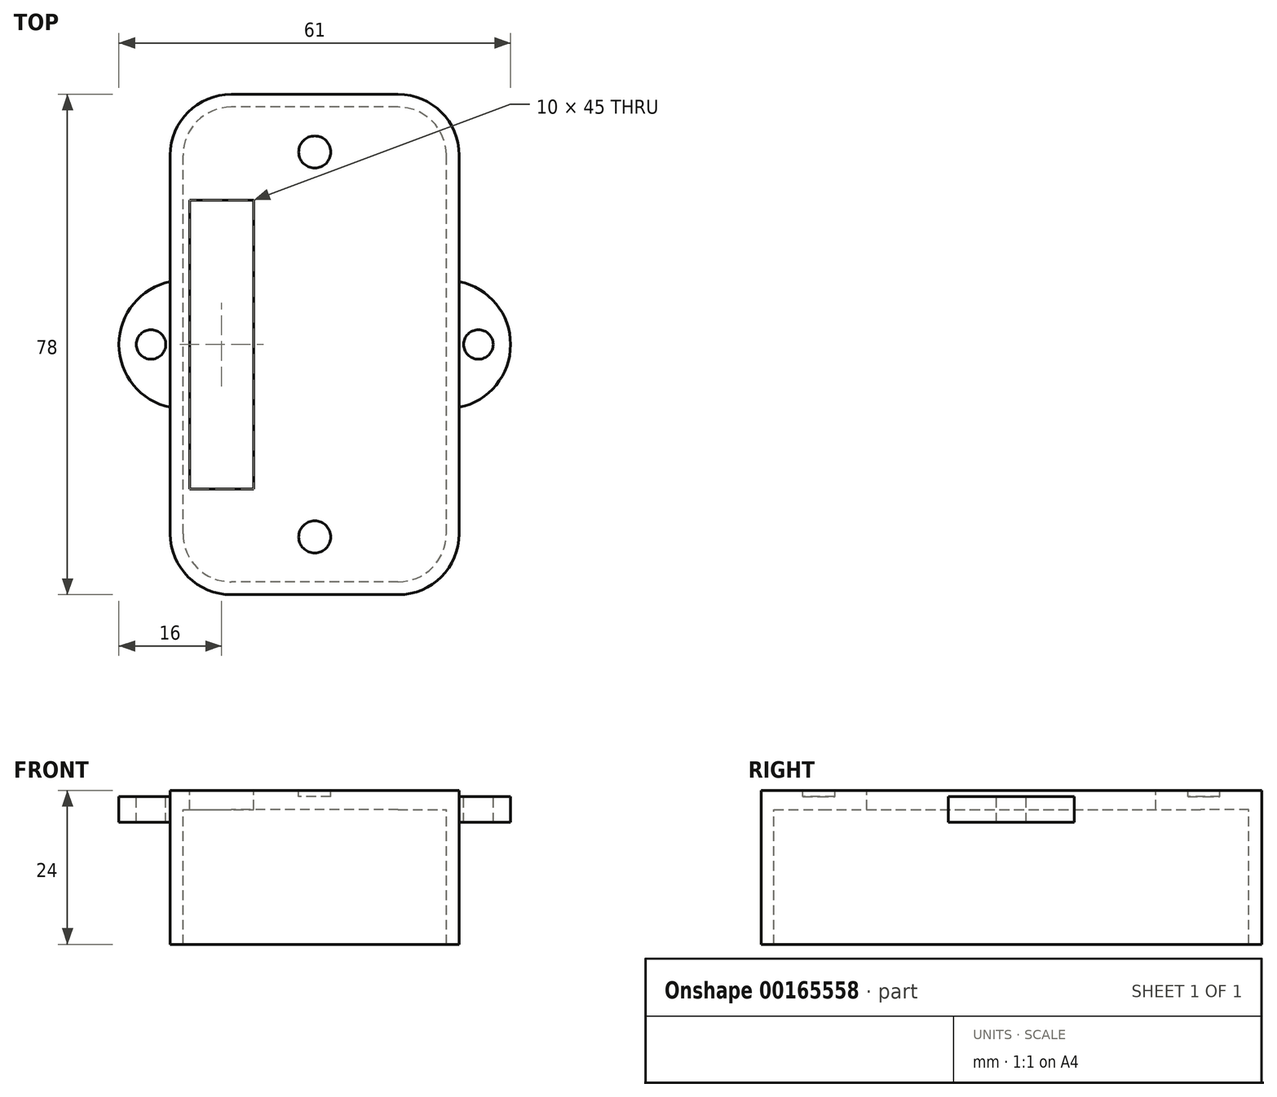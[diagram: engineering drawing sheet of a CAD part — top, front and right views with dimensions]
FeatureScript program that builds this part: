
annotation { "Feature Type Name" : "Feature", "Feature Type Description" : "" }
export const myFeature = defineFeature(function(context is Context, id is Id, definition is map)
    precondition{}
    {
        {
            var Q0;
            Q0=qCreatedBy(makeId("Top.planeOp"),FACE);
            var sketch = newSketch(context, id + "F0", { "sketchPlane" : qUnion([Q0])});
            skLineSegment(sketch, "E0.bottom", {"start": v(13, -37) * mm, "end": v(-13, -37) * mm});
            skLineSegment(sketch, "E0.top", {"start": v(13, 37) * mm, "end": v(-13, 37) * mm});
            skLineSegment(sketch, "E0.left", {"start": v(20.5, -29.5) * mm, "end": v(20.5, 29.5) * mm});
            skLineSegment(sketch, "E0.right", {"start": v(-20.5, -29.5) * mm, "end": v(-20.5, 29.5) * mm});
            skPoint(sketch, "E0.middle", {"position": v(0, 0) * mm});
            skPoint(sketch, "E1.visualSharp", {"position": v(-20.5, 37) * mm});
            skArc(sketch, "E1.filletArc", {"start": v(-13, 37) * mm, "mid": v(-18.3, 34.8) * mm, "end": v(-20.5, 29.5) * mm});
            skPoint(sketch, "E2.visualSharp", {"position": v(20.5, 37) * mm});
            skArc(sketch, "E2.filletArc", {"start": v(20.5, 29.5) * mm, "mid": v(18.3, 34.8) * mm, "end": v(13, 37) * mm});
            skPoint(sketch, "E3.visualSharp", {"position": v(20.5, -37) * mm});
            skArc(sketch, "E3.filletArc", {"start": v(13, -37) * mm, "mid": v(18.3, -34.8) * mm, "end": v(20.5, -29.5) * mm});
            skPoint(sketch, "E4.visualSharp", {"position": v(-20.5, -37) * mm});
            skArc(sketch, "E4.filletArc", {"start": v(-20.5, -29.5) * mm, "mid": v(-18.3, -34.8) * mm, "end": v(-13, -37) * mm});
            skArc(sketch, "E5.0", {"start": v(-22.5, -29.5) * mm, "mid": v(-19.72, -36.22) * mm, "end": v(-13, -39) * mm});
            skLineSegment(sketch, "E5.1", {"start": v(13, -39) * mm, "end": v(-13, -39) * mm});
            skLineSegment(sketch, "E5.2", {"start": v(-22.5, -29.5) * mm, "end": v(-22.5, 29.5) * mm});
            skArc(sketch, "E5.3", {"start": v(13, -39) * mm, "mid": v(19.72, -36.22) * mm, "end": v(22.5, -29.5) * mm});
            skArc(sketch, "E5.4", {"start": v(-13, 39) * mm, "mid": v(-19.72, 36.22) * mm, "end": v(-22.5, 29.5) * mm});
            skLineSegment(sketch, "E5.5", {"start": v(13, 39) * mm, "end": v(-13, 39) * mm});
            skArc(sketch, "E5.6", {"start": v(22.5, 29.5) * mm, "mid": v(19.72, 36.22) * mm, "end": v(13, 39) * mm});
            skLineSegment(sketch, "E5.7", {"start": v(22.5, -29.5) * mm, "end": v(22.5, 29.5) * mm});
            skPoint(sketch, "E6.centerSnap0", {"position": v(20.5, 0) * mm});
            skLineSegment(sketch, "E7", {"start": v(0, 0) * mm, "end": v(0, -30) * mm});
            skCircle(sketch, "E8", {"center": v(0, -30) * mm, "radius": 2.5 * mm});
            skCircle(sketch, "E9", {"center": v(0, 30) * mm, "radius": 2.5 * mm});
            skLineSegment(sketch, "E10.0", {"start": v(-19.5, 0) * mm, "end": v(-19.5, -22.5) * mm});
            skLineSegment(sketch, "E10.1", {"start": v(-19.5, 0) * mm, "end": v(-19.5, 22.5) * mm});
            skLineSegment(sketch, "E11.0", {"start": v(-9.5, 0) * mm, "end": v(-9.5, -22.5) * mm});
            skLineSegment(sketch, "E11.1", {"start": v(-9.5, 0) * mm, "end": v(-9.5, 22.5) * mm});
            skLineSegment(sketch, "E12", {"start": v(-19.5, 22.5) * mm, "end": v(-9.5, 22.5) * mm});
            skLineSegment(sketch, "E13", {"start": v(-19.5, -22.5) * mm, "end": v(-9.5, -22.5) * mm});
            skArc(sketch, "E14", {"start": v(22.5, -9.8) * mm, "mid": v(30.5, 0) * mm, "end": v(22.5, 9.8) * mm});
            skLineSegment(sketch, "E15", {"start": v(20.5, 0) * mm, "end": v(30.5, 0) * mm, "construction": true});
            skLineSegment(sketch, "E16", {"start": v(22.5, 0) * mm, "end": v(25.5, 0) * mm});
            skArc(sketch, "E17.MirrorCS", {"start": v(-22.5, -9.8) * mm, "mid": v(-30.5, 0) * mm, "end": v(-22.5, 9.8) * mm});
            skCircle(sketch, "E18", {"center": v(25.5, 0) * mm, "radius": 2.3 * mm});
            skCircle(sketch, "E19.MirrorC", {"center": v(-25.5, 0) * mm, "radius": 2.3 * mm});
            skSolve(sketch);
        }
        {
            var Q0;
            {var subQ5=sQuery(id+"F0.wireOp",EDGE,"K4ufOepT-8zNa-qbsu-fNWP-Ed5ITKJvoy9s.right");Q0=makeQuery(id+"F0.imprint","IMPRINT",FACE,{"disambiguationData":[TD([[makeQuery(id+"F0.imprint","IMPRINT",EDGE,{"derivedFrom":subQ5}),-1.0]])]});}
            var Q1;
            Q1=makeQuery(id+"F0.imprint","IMPRINT",FACE,{"disambiguationData":[TD([[makeQuery(id+"F0.imprint","IMPRINT",EDGE,{"derivedFrom":sQuery(id+"F0.wireOp",EDGE,"E0.top")}),1.0]])]});
            var Q2;
            Q2=makeQuery(id+"F0.imprint","IMPRINT",FACE,{"disambiguationData":[TD([[makeQuery(id+"F0.imprint","IMPRINT",EDGE,{"derivedFrom":sQuery(id+"F0.wireOp",EDGE,"E0.bottom")}),-1.0]])]});
            var Q3;
            {var subQ1=sQuery(id+"F0.wireOp",EDGE,"K4ufOepT-8zNa-qbsu-fNWP-Ed5ITKJvoy9s.left");var subQ3=sQuery(id+"F0.wireOp",EDGE,"29d169b9-53f3-4a3d-8caf-3cd1a107282e.0");var subQ4=makeQuery(id+"F0.imprint","INTERSECT",VERTEX,{"derivedFrom":[subQ3,subQ1]});Q3=makeQuery(id+"F0.imprint","IMPRINT",FACE,{"disambiguationData":[TD([[makeQuery(id+"F0.imprint","IMPRINT",EDGE,{"disambiguationData":[TD([[subQ4,-1.0]])],"derivedFrom":subQ3}),1.0]])]});}
            var Q4;
            {var subQ5=sQuery(id+"F0.wireOp",EDGE,"E0.right");var subQ6=sQuery(id+"F0.wireOp",EDGE,"rMVOqYj8-UWur-ThiU-V0Ca-l3qG7JqcSif2");var subQ7=makeQuery(id+"F0.imprint","INTERSECT",VERTEX,{"disambiguationData":[OD(1.0)],"derivedFrom":[subQ6,subQ5]});Q4=makeQuery(id+"F0.imprint","IMPRINT",FACE,{"disambiguationData":[TD([[makeQuery(id+"F0.imprint","IMPRINT",EDGE,{"disambiguationData":[TD([[subQ7,-1.0]])],"derivedFrom":subQ6}),1.0]])]});}
            var Q5;
            {var subQ6=sQuery(id+"F0.wireOp",EDGE,"rMVOqYj8-UWur-ThiU-V0Ca-l3qG7JqcSif2");var subQ11=sQuery(id+"F0.wireOp",EDGE,"E9");var subQ12=makeQuery(id+"F0.imprint","INTERSECT",VERTEX,{"disambiguationData":[OD(1.0)],"derivedFrom":[subQ6,subQ11]});Q5=makeQuery(id+"F0.imprint","IMPRINT",FACE,{"disambiguationData":[TD([[makeQuery(id+"F0.imprint","IMPRINT",EDGE,{"disambiguationData":[TD([[subQ12,-1.0]])],"derivedFrom":subQ6}),1.0]])]});}
            var Q6;
            {var subQ0=sQuery(id+"F0.wireOp",EDGE,"NyWOWrau-7Y7n-SZSj-ABbT-IQbbcggIcJFY");var subQ1=sQuery(id+"F0.wireOp",EDGE,"29d169b9-53f3-4a3d-8caf-3cd1a107282e.0");var subQ2=makeQuery(id+"F0.imprint","INTERSECT",VERTEX,{"disambiguationData":[OD(0.0)],"derivedFrom":[subQ1,subQ0]});Q6=makeQuery(id+"F0.imprint","IMPRINT",FACE,{"disambiguationData":[TD([[makeQuery(id+"F0.imprint","IMPRINT",EDGE,{"disambiguationData":[TD([[subQ2,-1.0]])],"derivedFrom":subQ1}),1.0]])]});}
            var Q7;
            {var subQ0=sQuery(id+"F0.wireOp",EDGE,"E9");var subQ1=sQuery(id+"F0.wireOp",EDGE,"McuKKnwl-45qK-wBoD-dtIe-04McT4cX6IDA");var subQ2=makeQuery(id+"F0.imprint","INTERSECT",VERTEX,{"disambiguationData":[OD(0.0)],"derivedFrom":[subQ1,subQ0]});Q7=makeQuery(id+"F0.imprint","IMPRINT",FACE,{"disambiguationData":[TD([[makeQuery(id+"F0.imprint","IMPRINT",EDGE,{"disambiguationData":[TD([[subQ2,1.0]])],"derivedFrom":subQ1}),1.0]])]});}
            var Q8;
            {var subQ0=sQuery(id+"F0.wireOp",EDGE,"E9");var subQ1=sQuery(id+"F0.wireOp",EDGE,"29d169b9-53f3-4a3d-8caf-3cd1a107282e.0");var subQ2=makeQuery(id+"F0.imprint","INTERSECT",VERTEX,{"disambiguationData":[OD(1.0)],"derivedFrom":[subQ1,subQ0]});Q8=makeQuery(id+"F0.imprint","IMPRINT",FACE,{"disambiguationData":[TD([[makeQuery(id+"F0.imprint","IMPRINT",EDGE,{"disambiguationData":[TD([[subQ2,-1.0]])],"derivedFrom":subQ1}),-1.0]])]});}
            var Q9;
            {var subQ0=sQuery(id+"F0.wireOp",EDGE,"NyWOWrau-7Y7n-SZSj-ABbT-IQbbcggIcJFY");var subQ1=sQuery(id+"F0.wireOp",EDGE,"29d169b9-53f3-4a3d-8caf-3cd1a107282e.0");var subQ2=makeQuery(id+"F0.imprint","INTERSECT",VERTEX,{"disambiguationData":[OD(0.0)],"derivedFrom":[subQ1,subQ0]});Q9=makeQuery(id+"F0.imprint","IMPRINT",FACE,{"disambiguationData":[TD([[makeQuery(id+"F0.imprint","IMPRINT",EDGE,{"disambiguationData":[TD([[subQ2,-1.0]])],"derivedFrom":subQ1}),-1.0]])]});}
            var Q10;
            {var subQ0=sQuery(id+"F0.wireOp",EDGE,"E9");var subQ1=sQuery(id+"F0.wireOp",EDGE,"rMVOqYj8-UWur-ThiU-V0Ca-l3qG7JqcSif2");var subQ2=makeQuery(id+"F0.imprint","INTERSECT",VERTEX,{"disambiguationData":[OD(1.0)],"derivedFrom":[subQ1,subQ0]});Q10=makeQuery(id+"F0.imprint","IMPRINT",FACE,{"disambiguationData":[TD([[makeQuery(id+"F0.imprint","IMPRINT",EDGE,{"disambiguationData":[TD([[subQ2,-1.0]])],"derivedFrom":subQ1}),-1.0]])]});}
            var Q11;
            {var subQ0=sQuery(id+"F0.wireOp",EDGE,"E0.left");var subQ1=sQuery(id+"F0.wireOp",EDGE,"rMVOqYj8-UWur-ThiU-V0Ca-l3qG7JqcSif2");var subQ2=makeQuery(id+"F0.imprint","INTERSECT",VERTEX,{"disambiguationData":[OD(0.0)],"derivedFrom":[subQ1,subQ0]});Q11=makeQuery(id+"F0.imprint","IMPRINT",FACE,{"disambiguationData":[TD([[makeQuery(id+"F0.imprint","IMPRINT",EDGE,{"disambiguationData":[TD([[subQ2,-1.0]])],"derivedFrom":subQ1}),-1.0]])]});}
            var Q12;
            {var subQ5=sQuery(id+"F0.wireOp",EDGE,"E0.left");var subQ6=sQuery(id+"F0.wireOp",EDGE,"rMVOqYj8-UWur-ThiU-V0Ca-l3qG7JqcSif2");var subQ7=makeQuery(id+"F0.imprint","INTERSECT",VERTEX,{"disambiguationData":[OD(0.0)],"derivedFrom":[subQ6,subQ5]});Q12=makeQuery(id+"F0.imprint","IMPRINT",FACE,{"disambiguationData":[TD([[makeQuery(id+"F0.imprint","IMPRINT",EDGE,{"disambiguationData":[TD([[subQ7,-1.0]])],"derivedFrom":subQ6}),1.0]])]});}
            var Q13;
            {var subQ0=sQuery(id+"F0.wireOp",EDGE,"E8");var subQ1=sQuery(id+"F0.wireOp",EDGE,"rMVOqYj8-UWur-ThiU-V0Ca-l3qG7JqcSif2");var subQ2=makeQuery(id+"F0.imprint","INTERSECT",VERTEX,{"disambiguationData":[OD(1.0)],"derivedFrom":[subQ1,subQ0]});Q13=makeQuery(id+"F0.imprint","IMPRINT",FACE,{"disambiguationData":[TD([[makeQuery(id+"F0.imprint","IMPRINT",EDGE,{"disambiguationData":[TD([[subQ2,-1.0]])],"derivedFrom":subQ1}),-1.0]])]});}
            var Q14;
            {var subQ3=sQuery(id+"F0.wireOp",EDGE,"E8");var subQ6=sQuery(id+"F0.wireOp",EDGE,"rMVOqYj8-UWur-ThiU-V0Ca-l3qG7JqcSif2");var subQ9=makeQuery(id+"F0.imprint","INTERSECT",VERTEX,{"disambiguationData":[OD(1.0)],"derivedFrom":[subQ6,subQ3]});Q14=makeQuery(id+"F0.imprint","IMPRINT",FACE,{"disambiguationData":[TD([[makeQuery(id+"F0.imprint","IMPRINT",EDGE,{"disambiguationData":[TD([[subQ9,-1.0]])],"derivedFrom":subQ6}),1.0]])]});}
            var Q15;
            {var subQ5=sQuery(id+"F0.wireOp",EDGE,"29d169b9-53f3-4a3d-8caf-3cd1a107282e.0");var subQ7=sQuery(id+"F0.wireOp",EDGE,"E8");var subQ9=makeQuery(id+"F0.imprint","INTERSECT",VERTEX,{"disambiguationData":[OD(1.0)],"derivedFrom":[subQ5,subQ7]});Q15=makeQuery(id+"F0.imprint","IMPRINT",FACE,{"disambiguationData":[TD([[makeQuery(id+"F0.imprint","IMPRINT",EDGE,{"disambiguationData":[TD([[subQ9,-1.0]])],"derivedFrom":subQ5}),1.0]])]});}
            var Q16;
            {var subQ0=sQuery(id+"F0.wireOp",EDGE,"E0.right");var subQ1=sQuery(id+"F0.wireOp",EDGE,"rMVOqYj8-UWur-ThiU-V0Ca-l3qG7JqcSif2");var subQ2=makeQuery(id+"F0.imprint","INTERSECT",VERTEX,{"disambiguationData":[OD(1.0)],"derivedFrom":[subQ1,subQ0]});Q16=makeQuery(id+"F0.imprint","IMPRINT",FACE,{"disambiguationData":[TD([[makeQuery(id+"F0.imprint","IMPRINT",EDGE,{"disambiguationData":[TD([[subQ2,-1.0]])],"derivedFrom":subQ1}),-1.0]])]});}
            var Q17;
            {var subQ0=sQuery(id+"F0.wireOp",EDGE,"E8");var subQ1=sQuery(id+"F0.wireOp",EDGE,"29d169b9-53f3-4a3d-8caf-3cd1a107282e.0");var subQ2=makeQuery(id+"F0.imprint","INTERSECT",VERTEX,{"disambiguationData":[OD(1.0)],"derivedFrom":[subQ1,subQ0]});Q17=makeQuery(id+"F0.imprint","IMPRINT",FACE,{"disambiguationData":[TD([[makeQuery(id+"F0.imprint","IMPRINT",EDGE,{"disambiguationData":[TD([[subQ2,-1.0]])],"derivedFrom":subQ1}),-1.0]])]});}
            var Q18;
            {var subQ0=sQuery(id+"F0.wireOp",EDGE,"eekdeFhl-0S7z-osEv-NQff-r2qTQL0hCeFo");var subQ1=sQuery(id+"F0.wireOp",EDGE,"29d169b9-53f3-4a3d-8caf-3cd1a107282e.0");var subQ2=makeQuery(id+"F0.imprint","INTERSECT",VERTEX,{"disambiguationData":[OD(0.0)],"derivedFrom":[subQ1,subQ0]});Q18=makeQuery(id+"F0.imprint","IMPRINT",FACE,{"disambiguationData":[TD([[makeQuery(id+"F0.imprint","IMPRINT",EDGE,{"disambiguationData":[TD([[subQ2,-1.0]])],"derivedFrom":subQ1}),-1.0]])]});}
            var Q19;
            {var subQ1=sQuery(id+"F0.wireOp",EDGE,"eekdeFhl-0S7z-osEv-NQff-r2qTQL0hCeFo");var subQ3=sQuery(id+"F0.wireOp",EDGE,"29d169b9-53f3-4a3d-8caf-3cd1a107282e.0");var subQ4=makeQuery(id+"F0.imprint","INTERSECT",VERTEX,{"disambiguationData":[OD(0.0)],"derivedFrom":[subQ3,subQ1]});Q19=makeQuery(id+"F0.imprint","IMPRINT",FACE,{"disambiguationData":[TD([[makeQuery(id+"F0.imprint","IMPRINT",EDGE,{"disambiguationData":[TD([[subQ4,-1.0]])],"derivedFrom":subQ3}),1.0]])]});}
            var Q20;
            {var subQ0=sQuery(id+"F0.wireOp",EDGE,"E8");var subQ1=sQuery(id+"F0.wireOp",EDGE,"gFNWuceC-rtio-qrhw-MDK2-LZ9uLdkySnU5");var subQ2=makeQuery(id+"F0.imprint","INTERSECT",VERTEX,{"disambiguationData":[OD(0.0)],"derivedFrom":[subQ1,subQ0]});Q20=makeQuery(id+"F0.imprint","IMPRINT",FACE,{"disambiguationData":[TD([[makeQuery(id+"F0.imprint","IMPRINT",EDGE,{"disambiguationData":[TD([[subQ2,1.0]])],"derivedFrom":subQ1}),1.0]])]});}
            var Q21;
            {var subQ0=sQuery(id+"F0.wireOp",EDGE,"E7");var subQ1=sQuery(id+"F0.wireOp",EDGE,"gFNWuceC-rtio-qrhw-MDK2-LZ9uLdkySnU5");var subQ2=makeQuery(id+"F0.imprint","INTERSECT",VERTEX,{"derivedFrom":[subQ1,subQ0]});Q21=makeQuery(id+"F0.imprint","IMPRINT",FACE,{"disambiguationData":[TD([[makeQuery(id+"F0.imprint","IMPRINT",EDGE,{"disambiguationData":[TD([[subQ2,1.0]])],"derivedFrom":subQ1}),1.0]])]});}
            extrude(context, id + "F1", {"entities" : qUnion([Q0, Q1, Q2, Q3, Q4, Q5, Q6, Q7, Q8, Q9, Q10, Q11, Q12, Q13, Q14, Q15, Q16, Q17, Q18, Q19, Q20, Q21]), "oppositeDirection" : true, "depth" : 2 * mm});
        }
        {
            var Q0;
            Q0=makeQuery(id+"F0.imprint","IMPRINT",FACE,{"disambiguationData":[TD([[makeQuery(id+"F0.imprint","IMPRINT",EDGE,{"derivedFrom":sQuery(id+"F0.wireOp",EDGE,"E0.top")}),-1.0]])]});
            var Q1;
            {var subQ0=sQuery(id+"F0.wireOp",EDGE,"E5.7");var subQ1=sQuery(id+"F0.wireOp",EDGE,"29d169b9-53f3-4a3d-8caf-3cd1a107282e.0");var subQ2=makeQuery(id+"F0.imprint","INTERSECT",VERTEX,{"disambiguationData":[OD(0.0)],"derivedFrom":[subQ1,subQ0]});Q1=makeQuery(id+"F0.imprint","IMPRINT",FACE,{"disambiguationData":[TD([[makeQuery(id+"F0.imprint","IMPRINT",EDGE,{"disambiguationData":[TD([[subQ2,-1.0]])],"derivedFrom":subQ1}),1.0]])]});}
            var Q2;
            {var subQ0=sQuery(id+"F0.wireOp",EDGE,"E0.left");var subQ1=sQuery(id+"F0.wireOp",EDGE,"rMVOqYj8-UWur-ThiU-V0Ca-l3qG7JqcSif2");var subQ2=makeQuery(id+"F0.imprint","INTERSECT",VERTEX,{"disambiguationData":[OD(0.0)],"derivedFrom":[subQ1,subQ0]});Q2=makeQuery(id+"F0.imprint","IMPRINT",FACE,{"disambiguationData":[TD([[makeQuery(id+"F0.imprint","IMPRINT",EDGE,{"disambiguationData":[TD([[subQ2,1.0]])],"derivedFrom":subQ1}),1.0]])]});}
            var Q3;
            {var subQ0=sQuery(id+"F0.wireOp",EDGE,"E0.left");var subQ1=sQuery(id+"F0.wireOp",EDGE,"rMVOqYj8-UWur-ThiU-V0Ca-l3qG7JqcSif2");var subQ2=makeQuery(id+"F0.imprint","INTERSECT",VERTEX,{"disambiguationData":[OD(0.0)],"derivedFrom":[subQ1,subQ0]});Q3=makeQuery(id+"F0.imprint","IMPRINT",FACE,{"disambiguationData":[TD([[makeQuery(id+"F0.imprint","IMPRINT",EDGE,{"disambiguationData":[TD([[subQ2,1.0]])],"derivedFrom":subQ1}),-1.0]])]});}
            var Q4;
            {var subQ0=sQuery(id+"F0.wireOp",EDGE,"E0.left");var subQ1=sQuery(id+"F0.wireOp",EDGE,"rMVOqYj8-UWur-ThiU-V0Ca-l3qG7JqcSif2");var subQ2=makeQuery(id+"F0.imprint","INTERSECT",VERTEX,{"disambiguationData":[OD(1.0)],"derivedFrom":[subQ1,subQ0]});Q4=makeQuery(id+"F0.imprint","IMPRINT",FACE,{"disambiguationData":[TD([[makeQuery(id+"F0.imprint","IMPRINT",EDGE,{"disambiguationData":[TD([[subQ2,-1.0]])],"derivedFrom":subQ1}),1.0]])]});}
            var Q5;
            {var subQ0=sQuery(id+"F0.wireOp",EDGE,"E0.left");var subQ1=sQuery(id+"F0.wireOp",EDGE,"rMVOqYj8-UWur-ThiU-V0Ca-l3qG7JqcSif2");var subQ2=makeQuery(id+"F0.imprint","INTERSECT",VERTEX,{"disambiguationData":[OD(1.0)],"derivedFrom":[subQ1,subQ0]});Q5=makeQuery(id+"F0.imprint","IMPRINT",FACE,{"disambiguationData":[TD([[makeQuery(id+"F0.imprint","IMPRINT",EDGE,{"disambiguationData":[TD([[subQ2,-1.0]])],"derivedFrom":subQ1}),-1.0]])]});}
            var Q6;
            Q6=makeQuery(id+"F0.imprint","IMPRINT",FACE,{"disambiguationData":[TD([[makeQuery(id+"F0.imprint","IMPRINT",EDGE,{"derivedFrom":sQuery(id+"F0.wireOp",EDGE,"E0.bottom")}),1.0]])]});
            var Q7;
            {var subQ0=sQuery(id+"F0.wireOp",EDGE,"E0.right");var subQ1=sQuery(id+"F0.wireOp",EDGE,"29d169b9-53f3-4a3d-8caf-3cd1a107282e.0");var subQ2=makeQuery(id+"F0.imprint","INTERSECT",VERTEX,{"disambiguationData":[OD(0.0)],"derivedFrom":[subQ1,subQ0]});Q7=makeQuery(id+"F0.imprint","IMPRINT",FACE,{"disambiguationData":[TD([[makeQuery(id+"F0.imprint","IMPRINT",EDGE,{"disambiguationData":[TD([[subQ2,-1.0]])],"derivedFrom":subQ1}),1.0]])]});}
            var Q8;
            {var subQ0=sQuery(id+"F0.wireOp",EDGE,"E5.2");var subQ1=sQuery(id+"F0.wireOp",EDGE,"rMVOqYj8-UWur-ThiU-V0Ca-l3qG7JqcSif2");var subQ2=makeQuery(id+"F0.imprint","INTERSECT",VERTEX,{"disambiguationData":[OD(1.0)],"derivedFrom":[subQ1,subQ0]});Q8=makeQuery(id+"F0.imprint","IMPRINT",FACE,{"disambiguationData":[TD([[makeQuery(id+"F0.imprint","IMPRINT",EDGE,{"disambiguationData":[TD([[subQ2,-1.0]])],"derivedFrom":subQ1}),1.0]])]});}
            var Q9;
            {var subQ0=sQuery(id+"F0.wireOp",EDGE,"E5.2");var subQ1=sQuery(id+"F0.wireOp",EDGE,"rMVOqYj8-UWur-ThiU-V0Ca-l3qG7JqcSif2");var subQ2=makeQuery(id+"F0.imprint","INTERSECT",VERTEX,{"disambiguationData":[OD(1.0)],"derivedFrom":[subQ1,subQ0]});Q9=makeQuery(id+"F0.imprint","IMPRINT",FACE,{"disambiguationData":[TD([[makeQuery(id+"F0.imprint","IMPRINT",EDGE,{"disambiguationData":[TD([[subQ2,-1.0]])],"derivedFrom":subQ1}),-1.0]])]});}
            var Q10;
            {var subQ0=sQuery(id+"F0.wireOp",EDGE,"E0.right");var subQ1=sQuery(id+"F0.wireOp",EDGE,"rMVOqYj8-UWur-ThiU-V0Ca-l3qG7JqcSif2");var subQ2=makeQuery(id+"F0.imprint","INTERSECT",VERTEX,{"disambiguationData":[OD(0.0)],"derivedFrom":[subQ1,subQ0]});Q10=makeQuery(id+"F0.imprint","IMPRINT",FACE,{"disambiguationData":[TD([[makeQuery(id+"F0.imprint","IMPRINT",EDGE,{"disambiguationData":[TD([[subQ2,-1.0]])],"derivedFrom":subQ1}),-1.0]])]});}
            var Q11;
            {var subQ0=sQuery(id+"F0.wireOp",EDGE,"E0.right");var subQ1=sQuery(id+"F0.wireOp",EDGE,"rMVOqYj8-UWur-ThiU-V0Ca-l3qG7JqcSif2");var subQ2=makeQuery(id+"F0.imprint","INTERSECT",VERTEX,{"disambiguationData":[OD(0.0)],"derivedFrom":[subQ1,subQ0]});Q11=makeQuery(id+"F0.imprint","IMPRINT",FACE,{"disambiguationData":[TD([[makeQuery(id+"F0.imprint","IMPRINT",EDGE,{"disambiguationData":[TD([[subQ2,-1.0]])],"derivedFrom":subQ1}),1.0]])]});}
            extrude(context, id + "F2", {"entities" : qUnion([Q0, Q1, Q2, Q3, Q4, Q5, Q6, Q7, Q8, Q9, Q10, Q11]), "operationType" : NewBodyOperationType.ADD, "oppositeDirection" : true, "depth" : 23 * mm});
        }
        {
            var Q0;
            Q0=makeQuery(id+"F1.opExtrude","CAP_FACE",FACE,{"disambiguationData":[OSD([sQuery(id+"F0.wireOp",EDGE,"E0.bottom"),sQuery(id+"F0.wireOp",EDGE,"E0.top"),sQuery(id+"F0.wireOp",EDGE,"E0.left"),sQuery(id+"F0.wireOp",EDGE,"E0.right"),sQuery(id+"F0.wireOp",EDGE,"E1.filletArc"),sQuery(id+"F0.wireOp",EDGE,"E2.filletArc"),sQuery(id+"F0.wireOp",EDGE,"E3.filletArc"),sQuery(id+"F0.wireOp",EDGE,"E4.filletArc"),sQuery(id+"F0.wireOp",EDGE,"K4ufOepT-8zNa-qbsu-fNWP-Ed5ITKJvoy9s.top"),sQuery(id+"F0.wireOp",EDGE,"K4ufOepT-8zNa-qbsu-fNWP-Ed5ITKJvoy9s.left"),sQuery(id+"F0.wireOp",EDGE,"K4ufOepT-8zNa-qbsu-fNWP-Ed5ITKJvoy9s.right"),sQuery(id+"F0.wireOp",EDGE,"f5cf270e-18e6-498c-ae04-22d9e1011c710.MirrorCS"),sQuery(id+"F0.wireOp",EDGE,"7aebd256-f6af-49ee-b425-2bd0de871cbd0.MirrorCS"),sQuery(id+"F0.wireOp",EDGE,"3b31796f-2ec3-44df-a347-8111aa19e6790.MirrorCS")])],"isStart":false});
            extrude(context, id + "F3", {"entities" : qUnion([Q0]), "operationType" : NewBodyOperationType.ADD, "oppositeDirection" : true, "depth" : 3 * mm});
        }
        {
            var Q0;
            Q0=qSketchRegion(id+"F0",true);
            var Q1;
            {var subQ3=sQuery(id+"F0.wireOp",EDGE,"E5.2");var subQ7=sQuery(id+"F0.wireOp",EDGE,"rMVOqYj8-UWur-ThiU-V0Ca-l3qG7JqcSif2");var subQ9=makeQuery(id+"F0.imprint","INTERSECT",VERTEX,{"disambiguationData":[OD(0.0)],"derivedFrom":[subQ7,subQ3]});Q1=makeQuery(id+"F0.imprint","IMPRINT",FACE,{"disambiguationData":[TD([[makeQuery(id+"F0.imprint","IMPRINT",EDGE,{"disambiguationData":[TD([[subQ9,-1.0]])],"derivedFrom":subQ7}),1.0]])]});}
            var Q2;
            {var subQ0=sQuery(id+"F0.wireOp",EDGE,"E5.2");var subQ1=sQuery(id+"F0.wireOp",EDGE,"29d169b9-53f3-4a3d-8caf-3cd1a107282e.0");var subQ2=makeQuery(id+"F0.imprint","INTERSECT",VERTEX,{"disambiguationData":[OD(0.0)],"derivedFrom":[subQ1,subQ0]});Q2=makeQuery(id+"F0.imprint","IMPRINT",FACE,{"disambiguationData":[TD([[makeQuery(id+"F0.imprint","IMPRINT",EDGE,{"disambiguationData":[TD([[subQ2,-1.0]])],"derivedFrom":subQ1}),1.0]])]});}
            var Q3;
            {var subQ0=sQuery(id+"F0.wireOp",EDGE,"OHaiA1tK-0UZL-TDxO-0ojw-HwiTPgMYLPrY");Q3=makeQuery(id+"F0.imprint","IMPRINT",FACE,{"disambiguationData":[TD([[makeQuery(id+"F0.imprint","IMPRINT",EDGE,{"derivedFrom":subQ0}),-1.0]])]});}
            var Q4;
            {var subQ0=sQuery(id+"F0.wireOp",EDGE,"29d169b9-53f3-4a3d-8caf-3cd1a107282e.0");var subQ1=makeQuery(id+"F0.imprint","INTERSECT",VERTEX,{"derivedFrom":[subQ0,sQuery(id+"F0.wireOp",EDGE,"OHaiA1tK-0UZL-TDxO-0ojw-HwiTPgMYLPrY")]});Q4=makeQuery(id+"F0.imprint","IMPRINT",FACE,{"disambiguationData":[TD([[makeQuery(id+"F0.imprint","IMPRINT",EDGE,{"disambiguationData":[TD([[subQ1,1.0]])],"derivedFrom":subQ0}),-1.0]])]});}
            var Q5;
            Q5=makeQuery(id+"F0.imprint","IMPRINT",FACE,{"disambiguationData":[TD([[makeQuery(id+"F0.imprint","IMPRINT",EDGE,{"derivedFrom":sQuery(id+"F0.wireOp",EDGE,"OHaiA1tK-0UZL-TDxO-0ojw-HwiTPgMYLPrY")}),1.0]])]});
            var Q6;
            {var subQ0=sQuery(id+"F0.wireOp",EDGE,"E6");var subQ1=sQuery(id+"F0.wireOp",EDGE,"29d169b9-53f3-4a3d-8caf-3cd1a107282e.0");var subQ2=makeQuery(id+"F0.imprint","INTERSECT",VERTEX,{"disambiguationData":[OD(0.0)],"derivedFrom":[subQ1,subQ0]});Q6=makeQuery(id+"F0.imprint","IMPRINT",FACE,{"disambiguationData":[TD([[makeQuery(id+"F0.imprint","IMPRINT",EDGE,{"disambiguationData":[TD([[subQ2,-1.0]])],"derivedFrom":subQ1}),1.0]])]});}
            var Q7;
            {var subQ0=sQuery(id+"F0.wireOp",EDGE,"JeTY6cms-RTc5-NGsc-flgO-fUigOLMTGN0w");Q7=makeQuery(id+"F0.imprint","IMPRINT",FACE,{"disambiguationData":[TD([[makeQuery(id+"F0.imprint","IMPRINT",EDGE,{"derivedFrom":subQ0}),-1.0]])]});}
            var Q8;
            Q8=makeQuery(id+"F0.imprint","IMPRINT",FACE,{"disambiguationData":[TD([[makeQuery(id+"F0.imprint","IMPRINT",EDGE,{"derivedFrom":sQuery(id+"F0.wireOp",EDGE,"JeTY6cms-RTc5-NGsc-flgO-fUigOLMTGN0w")}),1.0]])]});
            var Q9;
            {var subQ0=sQuery(id+"F0.wireOp",EDGE,"E5.7");var subQ1=sQuery(id+"F0.wireOp",EDGE,"rMVOqYj8-UWur-ThiU-V0Ca-l3qG7JqcSif2");var subQ9=makeQuery(id+"F0.imprint","INTERSECT",VERTEX,{"disambiguationData":[OD(0.0)],"derivedFrom":[subQ1,subQ0]});Q9=makeQuery(id+"F0.imprint","IMPRINT",FACE,{"disambiguationData":[TD([[makeQuery(id+"F0.imprint","IMPRINT",EDGE,{"disambiguationData":[TD([[subQ9,1.0]])],"derivedFrom":subQ1}),1.0]])]});}
            var Q10;
            {var subQ0=sQuery(id+"F0.wireOp",EDGE,"29d169b9-53f3-4a3d-8caf-3cd1a107282e.0");var subQ1=makeQuery(id+"F0.imprint","INTERSECT",VERTEX,{"derivedFrom":[subQ0,sQuery(id+"F0.wireOp",EDGE,"JeTY6cms-RTc5-NGsc-flgO-fUigOLMTGN0w")]});Q10=makeQuery(id+"F0.imprint","IMPRINT",FACE,{"disambiguationData":[TD([[makeQuery(id+"F0.imprint","IMPRINT",EDGE,{"disambiguationData":[TD([[subQ1,-1.0]])],"derivedFrom":subQ0}),-1.0]])]});}
            var Q11;
            {var subQ0=sQuery(id+"F0.wireOp",EDGE,"E9");var subQ1=sQuery(id+"F0.wireOp",EDGE,"rMVOqYj8-UWur-ThiU-V0Ca-l3qG7JqcSif2");var subQ2=makeQuery(id+"F0.imprint","INTERSECT",VERTEX,{"disambiguationData":[OD(0.0)],"derivedFrom":[subQ1,subQ0]});Q11=makeQuery(id+"F0.imprint","IMPRINT",FACE,{"disambiguationData":[TD([[makeQuery(id+"F0.imprint","IMPRINT",EDGE,{"disambiguationData":[TD([[subQ2,-1.0]])],"derivedFrom":subQ1}),-1.0]])]});}
            var Q12;
            {var subQ0=sQuery(id+"F0.wireOp",EDGE,"5E1CBNN6-1Jvb-JvIH-tPqv-O9M1JdmcJgxA");var subQ1=sQuery(id+"F0.wireOp",EDGE,"E9");var subQ2=makeQuery(id+"F0.imprint","INTERSECT",VERTEX,{"disambiguationData":[OD(0.0)],"derivedFrom":[subQ1,subQ0]});Q12=makeQuery(id+"F0.imprint","IMPRINT",FACE,{"disambiguationData":[TD([[makeQuery(id+"F0.imprint","IMPRINT",EDGE,{"disambiguationData":[TD([[subQ2,1.0]])],"derivedFrom":subQ1}),1.0]])]});}
            var Q13;
            {var subQ0=sQuery(id+"F0.wireOp",EDGE,"E9");var subQ1=sQuery(id+"F0.wireOp",EDGE,"rMVOqYj8-UWur-ThiU-V0Ca-l3qG7JqcSif2");var subQ2=makeQuery(id+"F0.imprint","INTERSECT",VERTEX,{"disambiguationData":[OD(0.0)],"derivedFrom":[subQ1,subQ0]});Q13=makeQuery(id+"F0.imprint","IMPRINT",FACE,{"disambiguationData":[TD([[makeQuery(id+"F0.imprint","IMPRINT",EDGE,{"disambiguationData":[TD([[subQ2,-1.0]])],"derivedFrom":subQ1}),1.0]])]});}
            var Q14;
            {var subQ0=sQuery(id+"F0.wireOp",EDGE,"E9");var subQ4=sQuery(id+"F0.wireOp",EDGE,"29d169b9-53f3-4a3d-8caf-3cd1a107282e.0");var subQ7=makeQuery(id+"F0.imprint","INTERSECT",VERTEX,{"disambiguationData":[OD(0.0)],"derivedFrom":[subQ4,subQ0]});Q14=makeQuery(id+"F0.imprint","IMPRINT",FACE,{"disambiguationData":[TD([[makeQuery(id+"F0.imprint","IMPRINT",EDGE,{"disambiguationData":[TD([[subQ7,-1.0]])],"derivedFrom":subQ4}),-1.0]])]});}
            var Q15;
            {var subQ0=sQuery(id+"F0.wireOp",EDGE,"E9");var subQ1=sQuery(id+"F0.wireOp",EDGE,"29d169b9-53f3-4a3d-8caf-3cd1a107282e.0");var subQ2=makeQuery(id+"F0.imprint","INTERSECT",VERTEX,{"disambiguationData":[OD(0.0)],"derivedFrom":[subQ1,subQ0]});Q15=makeQuery(id+"F0.imprint","IMPRINT",FACE,{"disambiguationData":[TD([[makeQuery(id+"F0.imprint","IMPRINT",EDGE,{"disambiguationData":[TD([[subQ2,-1.0]])],"derivedFrom":subQ1}),1.0]])]});}
            var Q16;
            {var subQ0=sQuery(id+"F0.wireOp",EDGE,"McuKKnwl-45qK-wBoD-dtIe-04McT4cX6IDA");var subQ1=makeQuery(id+"F0.imprint","INTERSECT",VERTEX,{"derivedFrom":[sQuery(id+"F0.wireOp",EDGE,"29d169b9-53f3-4a3d-8caf-3cd1a107282e.0"),subQ0]});Q16=makeQuery(id+"F0.imprint","IMPRINT",FACE,{"disambiguationData":[TD([[makeQuery(id+"F0.imprint","IMPRINT",EDGE,{"disambiguationData":[TD([[subQ1,1.0]])],"derivedFrom":subQ0}),1.0]])]});}
            var Q17;
            {var subQ0=sQuery(id+"F0.wireOp",EDGE,"McuKKnwl-45qK-wBoD-dtIe-04McT4cX6IDA");var subQ1=sQuery(id+"F0.wireOp",EDGE,"29d169b9-53f3-4a3d-8caf-3cd1a107282e.0");var subQ2=makeQuery(id+"F0.imprint","INTERSECT",VERTEX,{"derivedFrom":[subQ1,subQ0]});Q17=makeQuery(id+"F0.imprint","IMPRINT",FACE,{"disambiguationData":[TD([[makeQuery(id+"F0.imprint","IMPRINT",EDGE,{"disambiguationData":[TD([[subQ2,-1.0]])],"derivedFrom":subQ1}),1.0]])]});}
            var Q18;
            {var subQ0=sQuery(id+"F0.wireOp",EDGE,"E7");var subQ1=sQuery(id+"F0.wireOp",EDGE,"rMVOqYj8-UWur-ThiU-V0Ca-l3qG7JqcSif2");var subQ2=makeQuery(id+"F0.imprint","INTERSECT",VERTEX,{"derivedFrom":[subQ1,subQ0]});Q18=makeQuery(id+"F0.imprint","IMPRINT",FACE,{"disambiguationData":[TD([[makeQuery(id+"F0.imprint","IMPRINT",EDGE,{"disambiguationData":[TD([[subQ2,-1.0]])],"derivedFrom":subQ1}),1.0]])]});}
            var Q19;
            {var subQ3=sQuery(id+"F0.wireOp",EDGE,"E7");var subQ5=sQuery(id+"F0.wireOp",EDGE,"eekdeFhl-0S7z-osEv-NQff-r2qTQL0hCeFo");var subQ6=makeQuery(id+"F0.imprint","INTERSECT",VERTEX,{"disambiguationData":[OD(1.0)],"derivedFrom":[subQ5,subQ3]});Q19=makeQuery(id+"F0.imprint","IMPRINT",FACE,{"disambiguationData":[TD([[makeQuery(id+"F0.imprint","IMPRINT",EDGE,{"disambiguationData":[TD([[subQ6,-1.0]])],"derivedFrom":subQ5}),1.0]])]});}
            var Q20;
            {var subQ1=sQuery(id+"F0.wireOp",EDGE,"rMVOqYj8-UWur-ThiU-V0Ca-l3qG7JqcSif2");var subQ7=makeQuery(id+"F0.imprint","INTERSECT",VERTEX,{"derivedFrom":[subQ1,sQuery(id+"F0.wireOp",EDGE,"E7")]});Q20=makeQuery(id+"F0.imprint","IMPRINT",FACE,{"disambiguationData":[TD([[makeQuery(id+"F0.imprint","IMPRINT",EDGE,{"disambiguationData":[TD([[subQ7,1.0]])],"derivedFrom":subQ1}),-1.0]])]});}
            var Q21;
            {var subQ0=sQuery(id+"F0.wireOp",EDGE,"5E1CBNN6-1Jvb-JvIH-tPqv-O9M1JdmcJgxA");var subQ1=sQuery(id+"F0.wireOp",EDGE,"E8");var subQ2=makeQuery(id+"F0.imprint","INTERSECT",VERTEX,{"disambiguationData":[OD(0.0)],"derivedFrom":[subQ1,subQ0]});Q21=makeQuery(id+"F0.imprint","IMPRINT",FACE,{"disambiguationData":[TD([[makeQuery(id+"F0.imprint","IMPRINT",EDGE,{"disambiguationData":[TD([[subQ2,-1.0]])],"derivedFrom":subQ1}),1.0]])]});}
            var Q22;
            {var subQ0=sQuery(id+"F0.wireOp",EDGE,"E7");var subQ1=sQuery(id+"F0.wireOp",EDGE,"rMVOqYj8-UWur-ThiU-V0Ca-l3qG7JqcSif2");var subQ2=makeQuery(id+"F0.imprint","INTERSECT",VERTEX,{"derivedFrom":[subQ1,subQ0]});Q22=makeQuery(id+"F0.imprint","IMPRINT",FACE,{"disambiguationData":[TD([[makeQuery(id+"F0.imprint","IMPRINT",EDGE,{"disambiguationData":[TD([[subQ2,1.0]])],"derivedFrom":subQ1}),1.0]])]});}
            var Q23;
            {var subQ0=sQuery(id+"F0.wireOp",EDGE,"E8");var subQ5=sQuery(id+"F0.wireOp",EDGE,"eekdeFhl-0S7z-osEv-NQff-r2qTQL0hCeFo");var subQ7=makeQuery(id+"F0.imprint","INTERSECT",VERTEX,{"disambiguationData":[OD(0.0)],"derivedFrom":[subQ5,subQ0]});Q23=makeQuery(id+"F0.imprint","IMPRINT",FACE,{"disambiguationData":[TD([[makeQuery(id+"F0.imprint","IMPRINT",EDGE,{"disambiguationData":[TD([[subQ7,-1.0]])],"derivedFrom":subQ5}),1.0]])]});}
            var Q24;
            {var subQ0=sQuery(id+"F0.wireOp",EDGE,"E8");var subQ1=sQuery(id+"F0.wireOp",EDGE,"gFNWuceC-rtio-qrhw-MDK2-LZ9uLdkySnU5");var subQ2=makeQuery(id+"F0.imprint","INTERSECT",VERTEX,{"disambiguationData":[OD(0.0)],"derivedFrom":[subQ1,subQ0]});Q24=makeQuery(id+"F0.imprint","IMPRINT",FACE,{"disambiguationData":[TD([[makeQuery(id+"F0.imprint","IMPRINT",EDGE,{"disambiguationData":[TD([[subQ2,1.0]])],"derivedFrom":subQ0}),1.0]])]});}
            var Q25;
            {var subQ0=sQuery(id+"F0.wireOp",EDGE,"E8");var subQ1=sQuery(id+"F0.wireOp",EDGE,"gFNWuceC-rtio-qrhw-MDK2-LZ9uLdkySnU5");var subQ2=makeQuery(id+"F0.imprint","INTERSECT",VERTEX,{"disambiguationData":[OD(1.0)],"derivedFrom":[subQ1,subQ0]});Q25=makeQuery(id+"F0.imprint","IMPRINT",FACE,{"disambiguationData":[TD([[makeQuery(id+"F0.imprint","IMPRINT",EDGE,{"disambiguationData":[TD([[subQ2,-1.0]])],"derivedFrom":subQ0}),1.0]])]});}
            var Q26;
            {var subQ0=sQuery(id+"F0.wireOp",EDGE,"E8");var subQ1=sQuery(id+"F0.wireOp",EDGE,"29d169b9-53f3-4a3d-8caf-3cd1a107282e.0");var subQ2=makeQuery(id+"F0.imprint","INTERSECT",VERTEX,{"disambiguationData":[OD(1.0)],"derivedFrom":[subQ1,subQ0]});Q26=makeQuery(id+"F0.imprint","IMPRINT",FACE,{"disambiguationData":[TD([[makeQuery(id+"F0.imprint","IMPRINT",EDGE,{"disambiguationData":[TD([[subQ2,-1.0]])],"derivedFrom":subQ0}),1.0]])]});}
            var Q27;
            {var subQ0=sQuery(id+"F0.wireOp",EDGE,"E8");var subQ1=sQuery(id+"F0.wireOp",EDGE,"29d169b9-53f3-4a3d-8caf-3cd1a107282e.0");var subQ2=makeQuery(id+"F0.imprint","INTERSECT",VERTEX,{"disambiguationData":[OD(0.0)],"derivedFrom":[subQ1,subQ0]});Q27=makeQuery(id+"F0.imprint","IMPRINT",FACE,{"disambiguationData":[TD([[makeQuery(id+"F0.imprint","IMPRINT",EDGE,{"disambiguationData":[TD([[subQ2,1.0]])],"derivedFrom":subQ0}),1.0]])]});}
            extrude(context, id + "F4", {"entities" : qUnion([Q0, Q1, Q2, Q3, Q4, Q5, Q6, Q7, Q8, Q9, Q10, Q11, Q12, Q13, Q14, Q15, Q16, Q17, Q18, Q19, Q20, Q21, Q22, Q23, Q24, Q25, Q26, Q27]), "operationType" : NewBodyOperationType.ADD, "oppositeDirection" : true, "depth" : 2 * mm});
        }
        {
            var Q0;
            Q0=makeQuery(id+"F0.imprint","IMPRINT",FACE,{"disambiguationData":[TD([[makeQuery(id+"F0.imprint","IMPRINT",EDGE,{"derivedFrom":sQuery(id+"F0.wireOp",EDGE,"E0.bottom")}),1.0]])]});
            extrude(context, id + "F5", {"entities" : qUnion([Q0]), "operationType" : NewBodyOperationType.ADD, "depth" : 1 * mm});
        }
        {
            var Q0;
            {var subQ0=sQuery(id+"F0.wireOp",EDGE,"E5.2");var subQ1=sQuery(id+"F0.wireOp",EDGE,"E17.MirrorCS");var subQ2=sQuery(id+"F0.wireOp",EDGE,"E19.MirrorC");Q0=makeQuery(id+"F4.boolean.opBoolean","SPLIT",FACE,{"disambiguationData":[TD([makeQuery(id+"F2.opExtrude","SWEPT_FACE",FACE,{"disambiguationData":[OSD([subQ0])]})])],"derivedFrom":makeQuery(id+"F4.opExtrude","CAP_FACE",FACE,{"disambiguationData":[OSD([sQuery(id+"F0.wireOp",EDGE,"E0.bottom"),sQuery(id+"F0.wireOp",EDGE,"E0.top"),sQuery(id+"F0.wireOp",EDGE,"E0.left"),sQuery(id+"F0.wireOp",EDGE,"E0.right"),sQuery(id+"F0.wireOp",EDGE,"E1.filletArc"),sQuery(id+"F0.wireOp",EDGE,"E2.filletArc"),sQuery(id+"F0.wireOp",EDGE,"E3.filletArc"),sQuery(id+"F0.wireOp",EDGE,"E4.filletArc"),sQuery(id+"F0.wireOp",EDGE,"E5.0"),sQuery(id+"F0.wireOp",EDGE,"E5.1"),subQ0,sQuery(id+"F0.wireOp",EDGE,"E5.3"),sQuery(id+"F0.wireOp",EDGE,"E5.4"),sQuery(id+"F0.wireOp",EDGE,"E5.5"),sQuery(id+"F0.wireOp",EDGE,"E5.6"),sQuery(id+"F0.wireOp",EDGE,"E5.7"),sQuery(id+"F0.wireOp",EDGE,"E14"),subQ1,sQuery(id+"F0.wireOp",EDGE,"E18"),subQ2])],"isStart":false})});}
            var Q1;
            {var subQ0=sQuery(id+"F0.wireOp",EDGE,"E5.7");var subQ1=sQuery(id+"F0.wireOp",EDGE,"E18");var subQ2=sQuery(id+"F0.wireOp",EDGE,"E14");Q1=makeQuery(id+"F4.boolean.opBoolean","SPLIT",FACE,{"disambiguationData":[TD([makeQuery(id+"F2.opExtrude","SWEPT_FACE",FACE,{"disambiguationData":[OSD([subQ0])]})])],"derivedFrom":makeQuery(id+"F4.opExtrude","CAP_FACE",FACE,{"disambiguationData":[OSD([sQuery(id+"F0.wireOp",EDGE,"E0.bottom"),sQuery(id+"F0.wireOp",EDGE,"E0.top"),sQuery(id+"F0.wireOp",EDGE,"E0.left"),sQuery(id+"F0.wireOp",EDGE,"E0.right"),sQuery(id+"F0.wireOp",EDGE,"E1.filletArc"),sQuery(id+"F0.wireOp",EDGE,"E2.filletArc"),sQuery(id+"F0.wireOp",EDGE,"E3.filletArc"),sQuery(id+"F0.wireOp",EDGE,"E4.filletArc"),sQuery(id+"F0.wireOp",EDGE,"E5.0"),sQuery(id+"F0.wireOp",EDGE,"E5.1"),sQuery(id+"F0.wireOp",EDGE,"E5.2"),sQuery(id+"F0.wireOp",EDGE,"E5.3"),sQuery(id+"F0.wireOp",EDGE,"E5.4"),sQuery(id+"F0.wireOp",EDGE,"E5.5"),sQuery(id+"F0.wireOp",EDGE,"E5.6"),subQ0,subQ2,sQuery(id+"F0.wireOp",EDGE,"E17.MirrorCS"),subQ1,sQuery(id+"F0.wireOp",EDGE,"E19.MirrorC")])],"isStart":false})});}
            extrude(context, id + "F6", {"entities" : qUnion([Q0, Q1]), "operationType" : NewBodyOperationType.ADD, "depth" : 2 * mm});
        }
    });
